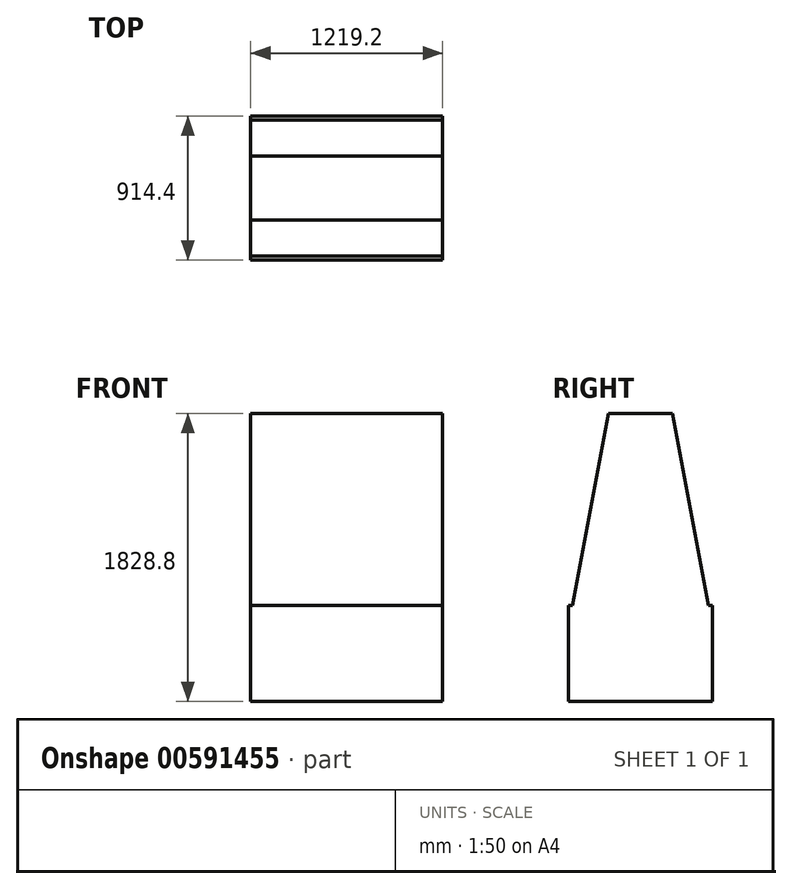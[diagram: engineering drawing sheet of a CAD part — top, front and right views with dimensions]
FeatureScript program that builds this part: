
annotation { "Feature Type Name" : "Feature", "Feature Type Description" : "" }
export const myFeature = defineFeature(function(context is Context, id is Id, definition is map)
    precondition{}
    {
        {
            var Q0;
            Q0=qCreatedBy(makeId("Right.planeOp"),FACE);
            var sketch = newSketch(context, id + "F0", { "sketchPlane" : qUnion([Q0])});
            skLineSegment(sketch, "E0.bottom", {"start": v(-376.9, 304.74) * mm, "end": v(-351.5, 304.74) * mm});
            skLineSegment(sketch, "E0.top", {"start": v(-376.9, -304.86) * mm, "end": v(537.5, -304.86) * mm});
            skLineSegment(sketch, "E0.left", {"start": v(-376.9, 304.74) * mm, "end": v(-376.9, -304.86) * mm});
            skLineSegment(sketch, "E0.right", {"start": v(537.5, 304.74) * mm, "end": v(537.5, -304.86) * mm});
            skLineSegment(sketch, "E1.top", {"start": v(-122.9, 1523.94) * mm, "end": v(283.5, 1523.94) * mm});
            skLineSegment(sketch, "E2", {"start": v(-122.9, 1523.94) * mm, "end": v(-351.5, 304.74) * mm});
            skLineSegment(sketch, "E3", {"start": v(283.5, 1523.94) * mm, "end": v(512.1, 304.74) * mm});
            skLineSegment(sketch, "E4.trimOffspring", {"start": v(512.1, 304.74) * mm, "end": v(537.5, 304.74) * mm});
            skSolve(sketch);
        }
        {
            var Q0;
            Q0 = qSketchRegion(id + "F0", true);
            extrude(context, id + "F1", {"entities" : qUnion([Q0]), "endBound" : BoundingType.SYMMETRIC, "depth" : 1219.2 * mm, "offsetDistance" : 25.4 * mm});
        }
    });
